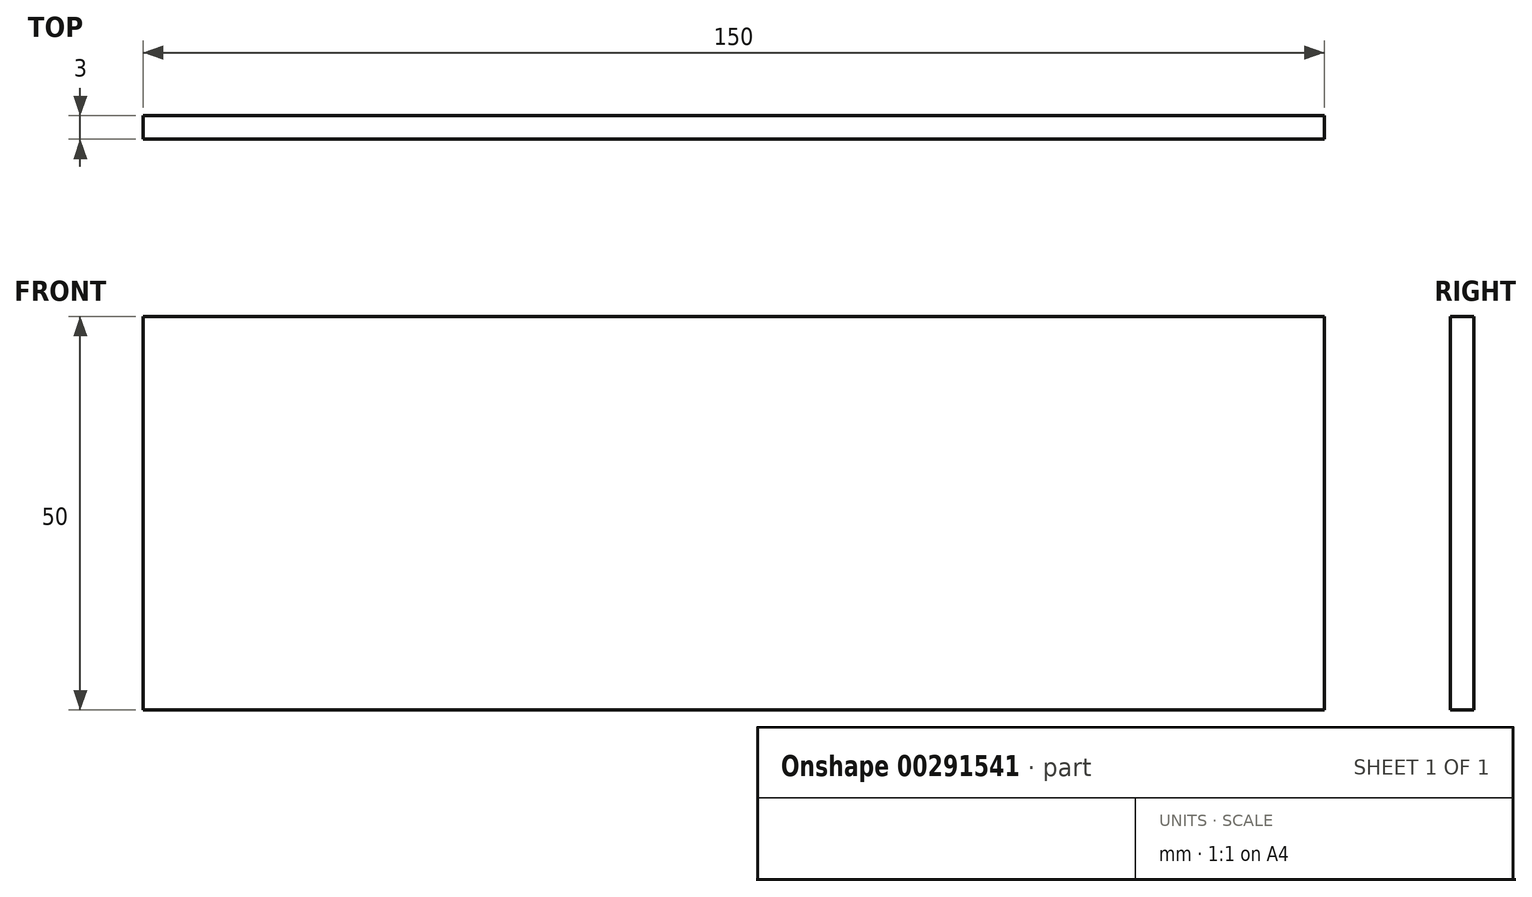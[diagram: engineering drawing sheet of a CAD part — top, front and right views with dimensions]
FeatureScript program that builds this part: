
annotation { "Feature Type Name" : "Feature", "Feature Type Description" : "" }
export const myFeature = defineFeature(function(context is Context, id is Id, definition is map)
    precondition{}
    {
        {
            var Q0;
            Q0=qCreatedBy(makeId("Front.planeOp"),FACE);
            var sketch = newSketch(context, id + "F0", { "sketchPlane" : qUnion([Q0])});
            skLineSegment(sketch, "E0.bottom", {"start": v(-75, 25) * mm, "end": v(75, 25) * mm});
            skLineSegment(sketch, "E0.top", {"start": v(-75, -25) * mm, "end": v(75, -25) * mm});
            skLineSegment(sketch, "E0.left", {"start": v(-75, 25) * mm, "end": v(-75, -25) * mm});
            skLineSegment(sketch, "E0.right", {"start": v(75, 25) * mm, "end": v(75, -25) * mm});
            skSolve(sketch);
        }
        {
            var Q0;
            Q0=makeQuery(id+"F0.imprint","IMPRINT",FACE,{"disambiguationData":[TD([[makeQuery(id+"F0.imprint","IMPRINT",EDGE,{"derivedFrom":sQuery(id+"F0.wireOp",EDGE,"E0.bottom")}),-1.0]])]});
            extrude(context, id + "F1", {"entities" : qUnion([Q0]), "endBound" : BoundingType.SYMMETRIC, "depth" : 3 * mm});
        }
    });
